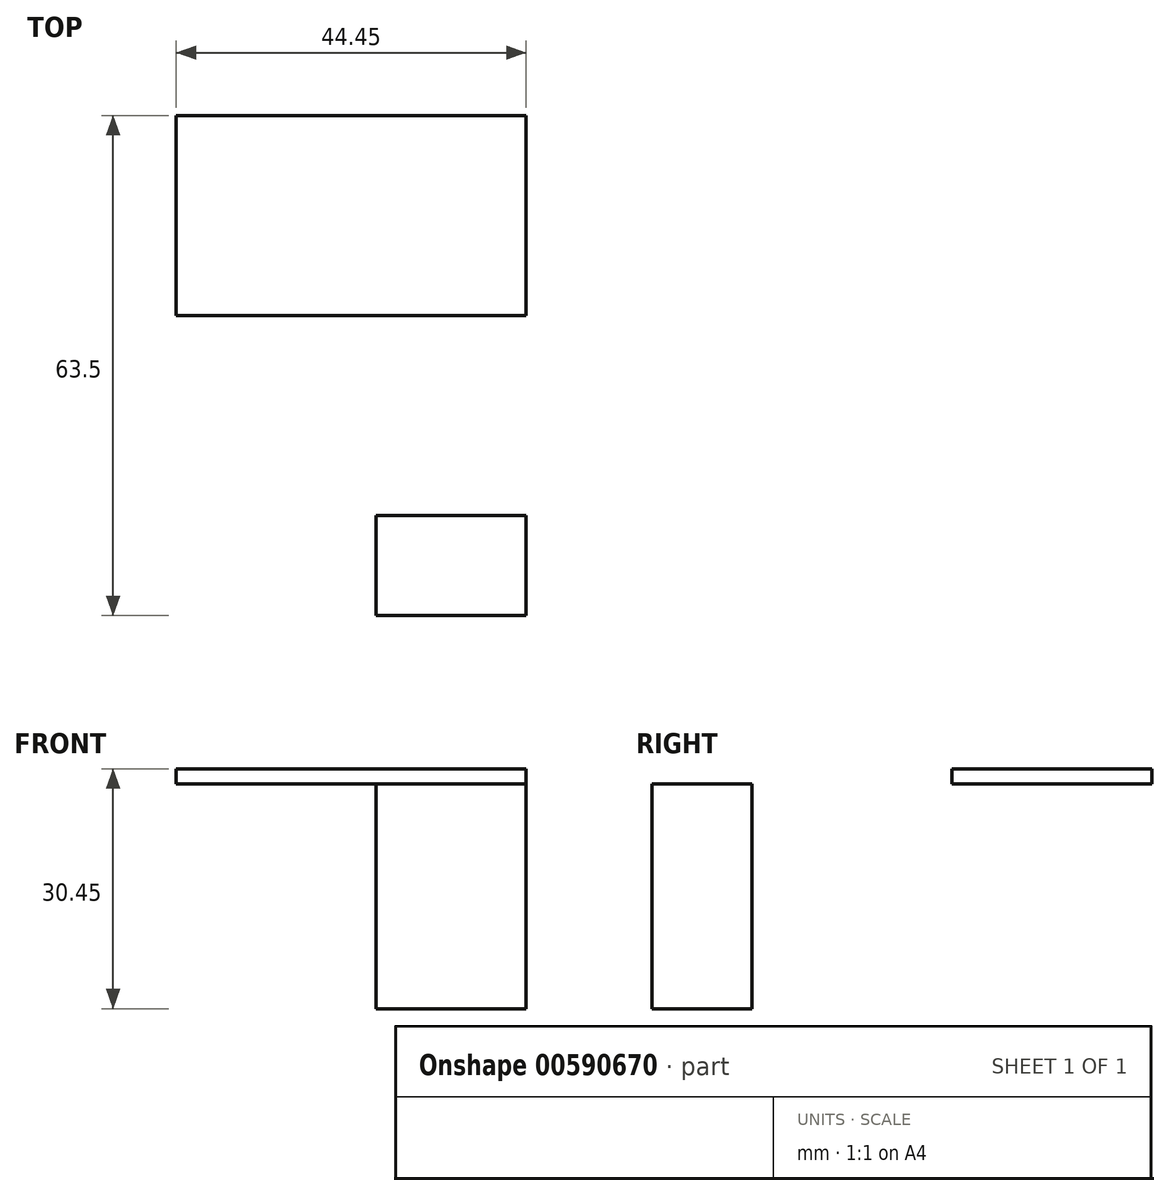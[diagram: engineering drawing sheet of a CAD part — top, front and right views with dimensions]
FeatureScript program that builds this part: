
annotation { "Feature Type Name" : "Feature", "Feature Type Description" : "" }
export const myFeature = defineFeature(function(context is Context, id is Id, definition is map)
    precondition{}
    {
        {
            var Q0;
            Q0=qCreatedBy(makeId("Top.planeOp"),FACE);
            var sketch = newSketch(context, id + "F0", { "sketchPlane" : qUnion([Q0])});
            skLineSegment(sketch, "E0.bottom", {"start": v(34.93, -31.75) * mm, "end": v(-34.93, -31.75) * mm});
            skLineSegment(sketch, "E0.top", {"start": v(34.93, 31.75) * mm, "end": v(-34.93, 31.75) * mm});
            skLineSegment(sketch, "E0.left", {"start": v(34.93, -31.75) * mm, "end": v(34.93, 31.75) * mm});
            skLineSegment(sketch, "E0.right", {"start": v(-34.93, -31.75) * mm, "end": v(-34.93, 31.75) * mm});
            skPoint(sketch, "E0.middle", {"position": v(0, 0) * mm});
            skLineSegment(sketch, "E1.bottom", {"start": v(34.93, -31.75) * mm, "end": v(15.88, -31.75) * mm});
            skLineSegment(sketch, "E1.top", {"start": v(34.93, -19.05) * mm, "end": v(15.88, -19.05) * mm});
            skLineSegment(sketch, "E1.left", {"start": v(34.93, -31.75) * mm, "end": v(34.93, -19.05) * mm});
            skLineSegment(sketch, "E1.right", {"start": v(15.88, -31.75) * mm, "end": v(15.88, -19.05) * mm});
            skSolve(sketch);
        }
        {
            var Q0;
            Q0=makeQuery(id+"F0.imprint","IMPRINT",FACE,{"disambiguationData":[TD([[makeQuery(id+"F0.imprint","IMPRINT",EDGE,{"derivedFrom":sQuery(id+"F0.wireOp",EDGE,"E0.bottom")}),-1.0]])]});
            extrude(context, id + "F1", {"entities" : qUnion([Q0]), "depth" : 28.57 * mm, "offsetDistance" : 25.4 * mm});
        }
        {
            var Q0;
            Q0=makeQuery(id+"F1.opExtrude","CAP_FACE",FACE,{"disambiguationData":[OSD([sQuery(id+"F0.wireOp",EDGE,"E0.bottom"),sQuery(id+"F0.wireOp",EDGE,"E0.top"),sQuery(id+"F0.wireOp",EDGE,"E0.left"),sQuery(id+"F0.wireOp",EDGE,"E0.right"),sQuery(id+"F0.wireOp",EDGE,"E1.top"),sQuery(id+"F0.wireOp",EDGE,"E1.right")])],"isStart":false});
            var sketch = newSketch(context, id + "F2", { "sketchPlane" : qUnion([Q0])});
            skLineSegment(sketch, "E2.bottom", {"start": v(34.93, 31.75) * mm, "end": v(-9.53, 31.75) * mm});
            skLineSegment(sketch, "E2.top", {"start": v(34.93, 6.35) * mm, "end": v(-9.52, 6.35) * mm});
            skLineSegment(sketch, "E2.left", {"start": v(34.93, 31.75) * mm, "end": v(34.93, 6.35) * mm});
            skLineSegment(sketch, "E2.right", {"start": v(-9.53, 31.75) * mm, "end": v(-9.52, 6.35) * mm});
            skSolve(sketch);
        }
        {
            var Q0;
            Q0 = qSketchRegion(id + "F2", true);
            extrude(context, id + "F3", {"entities" : qUnion([Q0]), "operationType" : NewBodyOperationType.ADD, "depth" : (1 + (7 / 8)) * mm, "offsetDistance" : 25.4 * mm});
        }
        {
            var Q0;
            Q0=makeQuery(id+"F3.boolean.opBoolean","MERGE",FACE,{"derivedFrom":[makeQuery(id+"F1.opExtrude","SWEPT_FACE",FACE,{"disambiguationData":[OSD([sQuery(id+"F0.wireOp",EDGE,"E0.top")])]}),makeQuery(id+"F3.opExtrude","SWEPT_FACE",FACE,{"disambiguationData":[OSD([sQuery(id+"F2.wireOp",EDGE,"E2.bottom")])]})]});
            var sketch = newSketch(context, id + "F4", { "sketchPlane" : qUnion([Q0])});
            skLineSegment(sketch, "E3.bottom", {"start": v(-34.93, 76.2) * mm, "end": v(-15.88, 76.2) * mm});
            skLineSegment(sketch, "E3.top", {"start": v(-34.93, 41.28) * mm, "end": v(-15.88, 41.28) * mm});
            skLineSegment(sketch, "E3.left", {"start": v(-34.93, 76.2) * mm, "end": v(-34.93, 41.28) * mm});
            skLineSegment(sketch, "E3.right", {"start": v(-15.88, 76.2) * mm, "end": v(-15.88, 41.28) * mm});
            skLineSegment(sketch, "E4", {"start": v(-15.88, 76.2) * mm, "end": v(-34.93, 41.28) * mm});
            skSolve(sketch);
        }
        {
            var Q0;
            Q0=makeQuery(id+"F4.imprint","IMPRINT",FACE,{"disambiguationData":[TD([[makeQuery(id+"F4.imprint","IMPRINT",EDGE,{"derivedFrom":sQuery(id+"F4.wireOp",EDGE,"E3.bottom")}),-1.0]])]});
            extrude(context, id + "F5", {"entities" : qUnion([Q0]), "operationType" : NewBodyOperationType.REMOVE, "oppositeDirection" : true, "depth" : 25.4 * mm, "offsetDistance" : 25.4 * mm});
        }
    });
